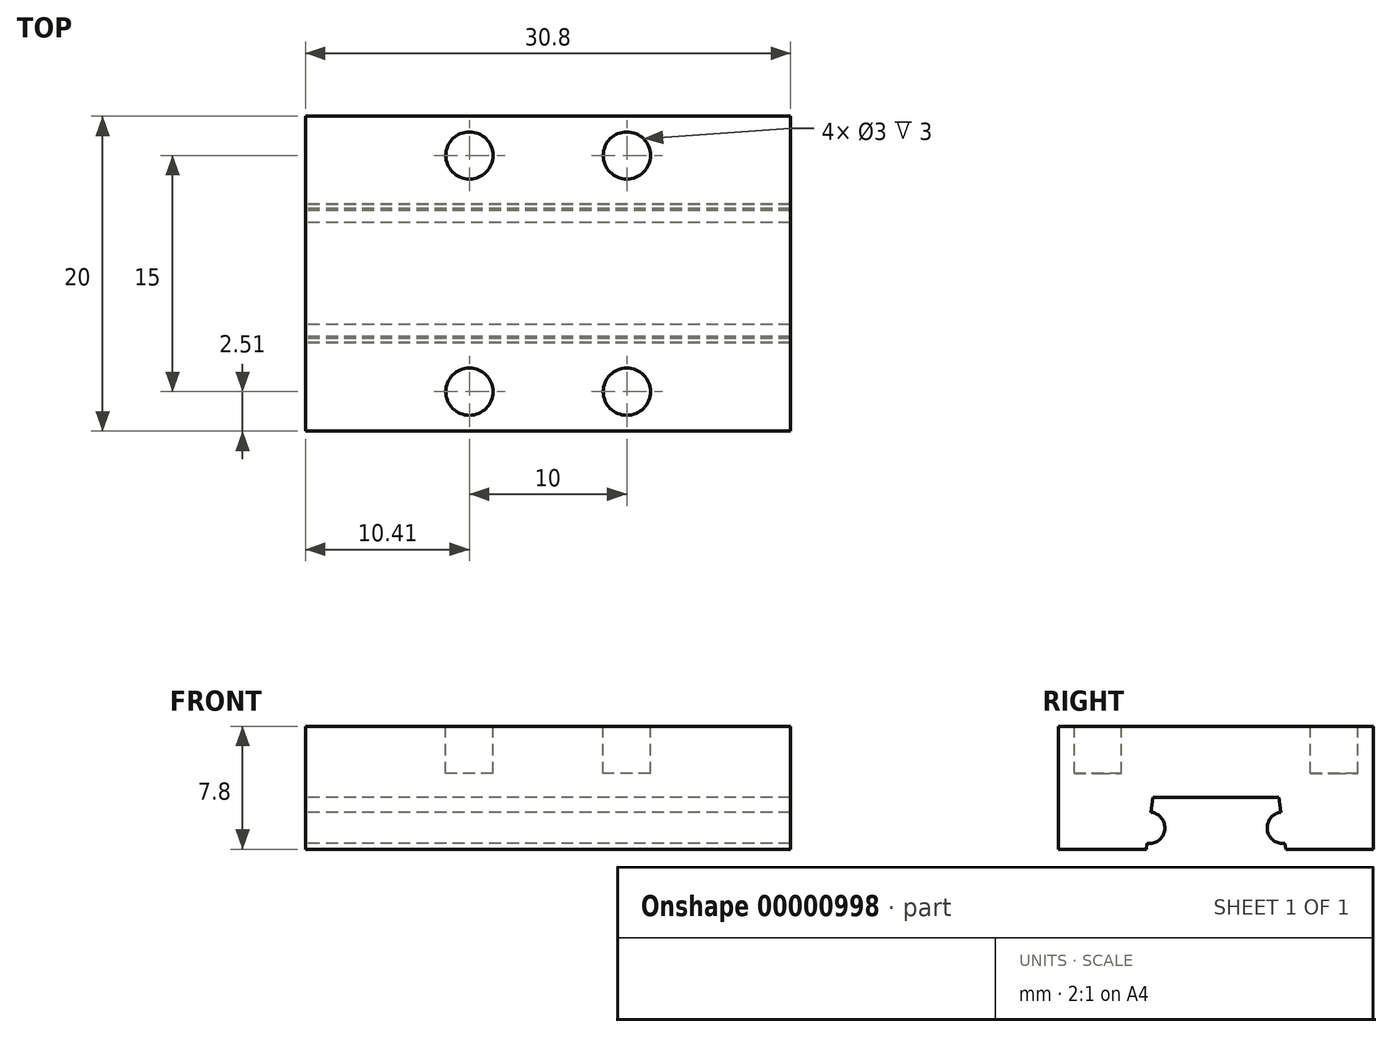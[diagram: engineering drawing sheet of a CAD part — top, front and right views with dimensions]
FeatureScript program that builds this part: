
annotation { "Feature Type Name" : "Feature", "Feature Type Description" : "" }
export const myFeature = defineFeature(function(context is Context, id is Id, definition is map)
    precondition{}
    {
        {
            var Q0;
            Q0=qCreatedBy(makeId("Top.planeOp"),FACE);
            var sketch = newSketch(context, id + "F0", { "sketchPlane" : qUnion([Q0])});
            skLineSegment(sketch, "E0.bottom", {"start": v(-15.4, 10) * mm, "end": v(15.4, 10) * mm});
            skLineSegment(sketch, "E0.top", {"start": v(-15.4, -10) * mm, "end": v(15.4, -10) * mm});
            skLineSegment(sketch, "E0.left", {"start": v(-15.4, 10) * mm, "end": v(-15.4, -10) * mm});
            skLineSegment(sketch, "E0.right", {"start": v(15.4, 10) * mm, "end": v(15.4, -10) * mm});
            skSolve(sketch);
        }
        {
            var Q0;
            Q0=makeQuery(id+"F0.imprint","IMPRINT",FACE,{"disambiguationData":[TD([[makeQuery(id+"F0.imprint","IMPRINT",EDGE,{"derivedFrom":sQuery(id+"F0.wireOp",EDGE,"E0.bottom")}),-1.0]])]});
            var Q1;
            Q1=makeQuery(id+"F0.imprint","IMPRINT",FACE,{"disambiguationData":[TD([[makeQuery(id+"F0.imprint","IMPRINT",EDGE,{"derivedFrom":sQuery(id+"F0.wireOp",EDGE,"86f441d8-751f-48c4-88ce-a573c146ee8f")}),1.0]])]});
            var Q2;
            Q2=makeQuery(id+"F0.imprint","IMPRINT",FACE,{"disambiguationData":[TD([[makeQuery(id+"F0.imprint","IMPRINT",EDGE,{"derivedFrom":sQuery(id+"F0.wireOp",EDGE,"2ad78070-b090-4811-a03b-6271cdfec725")}),1.0]])]});
            var Q3;
            Q3=makeQuery(id+"F0.imprint","IMPRINT",FACE,{"disambiguationData":[TD([[makeQuery(id+"F0.imprint","IMPRINT",EDGE,{"derivedFrom":sQuery(id+"F0.wireOp",EDGE,"73bcb557-e887-40bc-8d05-2d92c4f53819")}),1.0]])]});
            var Q4;
            Q4=makeQuery(id+"F0.imprint","IMPRINT",FACE,{"disambiguationData":[TD([[makeQuery(id+"F0.imprint","IMPRINT",EDGE,{"derivedFrom":sQuery(id+"F0.wireOp",EDGE,"64a830b0-1864-4f95-880d-4b630811c23e")}),1.0]])]});
            extrude(context, id + "F1", {"entities" : qUnion([Q0, Q1, Q2, Q3, Q4]), "depth" : 7.8 * mm});
        }
        {
            var Q0;
            Q0=makeQuery(id+"F1.opExtrude","SWEPT_FACE",FACE,{"disambiguationData":[OSD([sQuery(id+"F0.wireOp",EDGE,"E0.left")])]});
            var sketch = newSketch(context, id + "F2", { "sketchPlane" : qUnion([Q0])});
            skLineSegment(sketch, "E1", {"start": v(-4, 3.3) * mm, "end": v(4, 3.3) * mm});
            skLineSegment(sketch, "E2", {"start": v(-4.5, -0.6) * mm, "end": v(4.5, -0.6) * mm});
            skLineSegment(sketch, "E3", {"start": v(-4, 3.3) * mm, "end": v(-4.12, 2.35) * mm});
            skLineSegment(sketch, "E4", {"start": v(4, 3.3) * mm, "end": v(4.12, 2.35) * mm});
            skArc(sketch, "E5", {"start": v(-4.38, 0.36) * mm, "mid": v(-3.26, 1.23) * mm, "end": v(-4.12, 2.35) * mm});
            skArc(sketch, "E6", {"start": v(4.12, 2.35) * mm, "mid": v(3.26, 1.23) * mm, "end": v(4.38, 0.36) * mm});
            skLineSegment(sketch, "E7.trimOffspring", {"start": v(-4.38, 0.36) * mm, "end": v(-4.5, -0.6) * mm});
            skLineSegment(sketch, "E8.trimOffspring", {"start": v(4.38, 0.36) * mm, "end": v(4.5, -0.6) * mm});
            skSolve(sketch);
        }
        {
            var Q0;
            {var subQ5=sQuery(id+"F2.wireOp",EDGE,"E2");Q0=makeQuery(id+"F2.imprint","IMPRINT",FACE,{"disambiguationData":[TD([[makeQuery(id+"F2.imprint","IMPRINT",EDGE,{"derivedFrom":subQ5}),1.0]])]});}
            var Q1;
            Q1=makeQuery(id+"F2.imprint","IMPRINT",FACE,{"disambiguationData":[TD([[makeQuery(id+"F2.imprint","IMPRINT",EDGE,{"derivedFrom":sQuery(id+"F2.wireOp",EDGE,"E1")}),-1.0]])]});
            extrude(context, id + "F3", {"entities" : qUnion([Q0, Q1]), "operationType" : NewBodyOperationType.REMOVE, "endBound" : BoundingType.THROUGH_ALL, "oppositeDirection" : true, "depth" : 25.4 * mm});
        }
        {
            var Q0;
            Q0=makeQuery(id+"F1.opExtrude","CAP_FACE",FACE,{"disambiguationData":[OSD([sQuery(id+"F0.wireOp",EDGE,"E0.bottom"),sQuery(id+"F0.wireOp",EDGE,"E0.top"),sQuery(id+"F0.wireOp",EDGE,"E0.left"),sQuery(id+"F0.wireOp",EDGE,"E0.right")])],"isStart":false});
            var sketch = newSketch(context, id + "F4", { "sketchPlane" : qUnion([Q0])});
            skCircle(sketch, "E9", {"center": v(-5, 7.5) * mm, "radius": 1.5 * mm});
            skCircle(sketch, "E10", {"center": v(5, 7.5) * mm, "radius": 1.5 * mm});
            skCircle(sketch, "E11", {"center": v(5, -7.5) * mm, "radius": 1.5 * mm});
            skCircle(sketch, "E12", {"center": v(-5, -7.5) * mm, "radius": 1.5 * mm});
            skSolve(sketch);
        }
        {
            var Q0;
            {Q0=qUnion([makeQuery(id+"F4.imprint","IMPRINT",FACE,{"disambiguationData":[TD([[makeQuery(id+"F4.imprint","IMPRINT",EDGE,{"derivedFrom":sQuery(id+"F4.wireOp",EDGE,"E9")}),1.0]])]}),makeQuery(id+"F4.imprint","IMPRINT",FACE,{"disambiguationData":[TD([[makeQuery(id+"F4.imprint","IMPRINT",EDGE,{"derivedFrom":sQuery(id+"F4.wireOp",EDGE,"E10")}),1.0]])]}),makeQuery(id+"F4.imprint","IMPRINT",FACE,{"disambiguationData":[TD([[makeQuery(id+"F4.imprint","IMPRINT",EDGE,{"derivedFrom":sQuery(id+"F4.wireOp",EDGE,"E11")}),1.0]])]}),makeQuery(id+"F4.imprint","IMPRINT",FACE,{"disambiguationData":[TD([[makeQuery(id+"F4.imprint","IMPRINT",EDGE,{"derivedFrom":sQuery(id+"F4.wireOp",EDGE,"E12")}),1.0]])]})]);}
            extrude(context, id + "F5", {"entities" : qUnion([Q0]), "operationType" : NewBodyOperationType.REMOVE, "oppositeDirection" : true, "depth" : 3 * mm});
        }
    });
